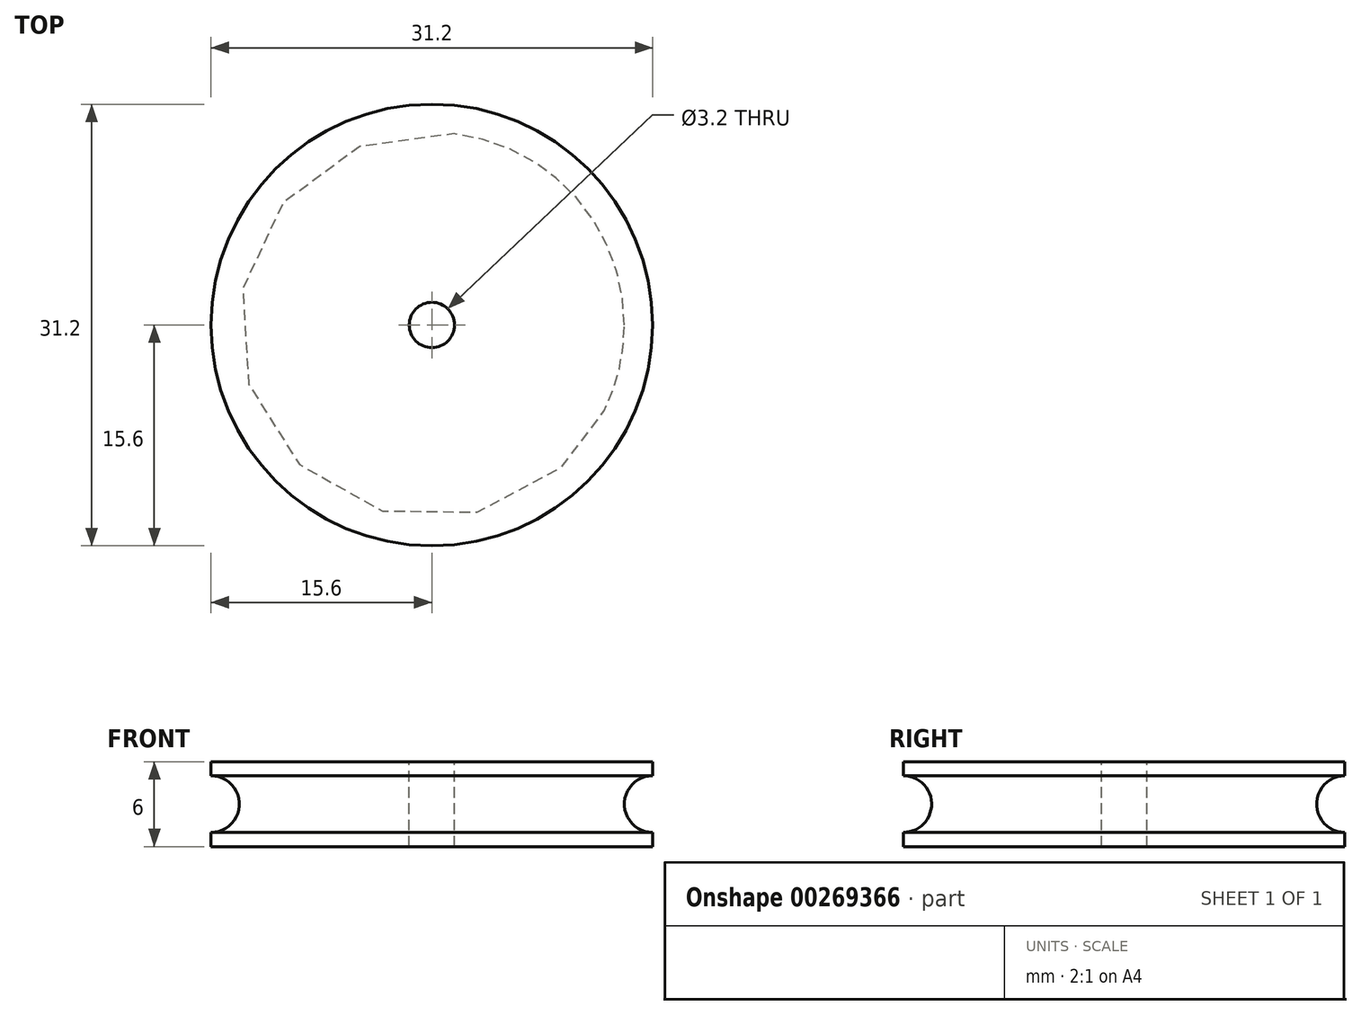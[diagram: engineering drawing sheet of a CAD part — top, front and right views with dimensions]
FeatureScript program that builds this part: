
annotation { "Feature Type Name" : "Feature", "Feature Type Description" : "" }
export const myFeature = defineFeature(function(context is Context, id is Id, definition is map)
    precondition{}
    {
        {
            var Q0;
            Q0=qCreatedBy(makeId("Front.planeOp"),FACE);
            var sketch = newSketch(context, id + "F0", { "sketchPlane" : qUnion([Q0])});
            skLineSegment(sketch, "E0", {"start": v(0, 3) * mm, "end": v(0, -3) * mm});
            skLineSegment(sketch, "E1", {"start": v(1.6, 3) * mm, "end": v(15.6, 3) * mm});
            skLineSegment(sketch, "E2", {"start": v(1.6, -3) * mm, "end": v(15.6, -3) * mm});
            skLineSegment(sketch, "E3", {"start": v(1.6, 3) * mm, "end": v(1.6, -3) * mm});
            skLineSegment(sketch, "E4", {"start": v(15.6, 3) * mm, "end": v(15.6, 2) * mm});
            skLineSegment(sketch, "E5", {"start": v(15.6, -3) * mm, "end": v(15.6, -2) * mm});
            skArc(sketch, "E6", {"start": v(15.6, 2) * mm, "mid": v(13.6, 0) * mm, "end": v(15.6, -2) * mm});
            skPoint(sketch, "E6.third.point", {"position": v(17.6, 0) * mm});
            skSolve(sketch);
        }
        {
            var Q0;
            Q0=makeQuery(id+"F0.imprint","IMPRINT",FACE,{"disambiguationData":[TD([[makeQuery(id+"F0.imprint","IMPRINT",EDGE,{"derivedFrom":sQuery(id+"F0.wireOp",EDGE,"E1")}),-1.0]])]});
            var Q1;
            Q1=sQuery(id+"F0.wireOp",EDGE,"E0");
            revolve(context, id + "F1", {"entities" : qUnion([Q0]), "axis" : qUnion([Q1]), "revolveType" : RevolveType.FULL});
        }
    });
